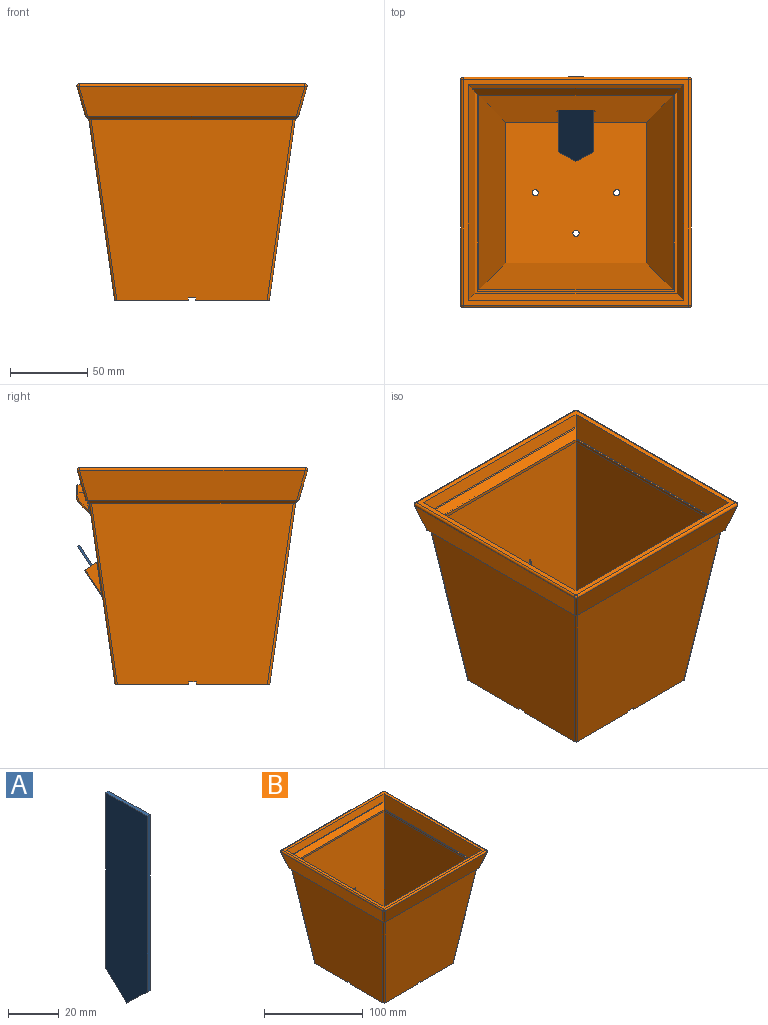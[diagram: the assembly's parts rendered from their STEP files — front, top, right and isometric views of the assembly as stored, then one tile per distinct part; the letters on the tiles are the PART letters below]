
ASSEMBLY  parts=2 mates=1
PART A: 7 faces, bbox 1.7x23x96 mm
  f0: plane 11.5x11mm, normal (0,-0.69,-0.72), area 26.3mm2, adj f1,f4,f5,f6
  f1: plane 11.5x11mm, normal (0,0.69,-0.72), area 26.3mm2, adj f0,f2,f5,f6
  f2: plane 85x1.65mm, normal (0,1,0), area 140.2mm2, adj f1,f3,f5,f6
  f3: plane 23x1.65mm, normal (0,0,1), area 37.9mm2, adj f2,f4,f5,f6
  f4: plane 85x1.65mm, normal (0,-1,0), area 140.2mm2, adj f0,f3,f5,f6
  f5: plane 96x23mm, normal (1,0,0), area 2081.5mm2, adj f0,f1,f2,f3,f4
  f6: plane 96x23mm, normal (-1,0,0), area 2081.5mm2, adj f0,f1,f2,f3,f4
PART B: 110 faces, bbox 149.1x150x140.2 mm
  f0: plane 11.53x6.95mm, normal (1,0,0), area 39.9mm2, adj f3,f19,f73,f95,f96,f97,f107
  f1: plane 11.53x6.95mm, normal (-1,0,0), area 39.9mm2, adj f19,f47,f73,f100,f102,f104,f109
  f2: plane 130.47x117.03mm, normal (0,0.99,-0.14), area 12611mm2, adj f3,f8,f16,f44,f47,f49,f53,f69
  f3: plane 62.79x2.2mm, normal (0,0.66,-0.76), area 170.1mm2, adj f0,f2,f19,f53,f56,f60,f96
  f4: plane 47.5x47.5mm, normal (0,0,-1), area 2255.8mm2, adj f5,f7,f11,f51,f72
  f5: plane 130.47x117.03mm, normal (0,-0.99,-0.14), area 13439.6mm2, adj f4,f10,f44,f46,f51,f66,f71,f72
  f6: plane 47.71x1.5mm, normal (0,1,0), area 71.4mm2, adj f10,f15,f44,f71
  f7: plane 47.71x1.5mm, normal (0,1,0), area 71.4mm2, adj f4,f11,f44,f72
  f8: plane 47.5x47.5mm, normal (0,0,-1), area 2255.8mm2, adj f2,f9,f15,f53,f69
  f9: plane 47.71x1.5mm, normal (0,-1,0), area 71.4mm2, adj f8,f15,f44,f69
  f10: plane 47.5x47.5mm, normal (0,0,-1), area 2255.8mm2, adj f5,f6,f15,f66,f71
  f11: plane 130.47x117.03mm, normal (-0.99,0,-0.14), area 13439.6mm2, adj f4,f7,f16,f43,f44,f48,f49,f51
  f12: plane 127.61x127.61mm, normal (0,0,1), area 379.8mm2, adj f27,f28,f30,f31,f32,f33,f39,f41
  f13: plane 139.58x7.5mm, normal (0,-0.96,0.28), area 1073.7mm2, adj f21,f24,f25,f42
  f14: plane 134.74x6.66mm, normal (0,-0.96,0.28), area 902.4mm2, adj f22,f24,f25,f40,f105
  f15: plane 130.47x117.03mm, normal (0.99,0,-0.14), area 13439.6mm2, adj f6,f8,f9,f10,f44,f45,f53,f66
  f16: plane 47.5x47.5mm, normal (0,0,-1), area 2255.8mm2, adj f2,f11,f43,f49,f70
  f17: plane 146x19.24mm, normal (0,-0.96,-0.28), area 2814.1mm2, adj f46,f57,f63,f67
  f18: plane 146x19.24mm, normal (0.96,0,-0.28), area 2814.1mm2, adj f45,f60,f64,f67
  f19: plane 146x19.24mm, normal (0,0.96,-0.28), area 2721.1mm2, adj f0,f1,f3,f47,f52,f59,f60,f73
  f20: plane 146x19.24mm, normal (-0.96,0,-0.28), area 2814.1mm2, adj f48,f52,f57,f58
  f21: plane 146x146mm, normal (0,0,1), area 1832.1mm2, adj f13,f23,f24,f25,f58,f59,f63,f64
  f22: plane 130.79x130.79mm, normal (0,0,1), area 819.2mm2, adj f14,f23,f24,f25,f29,f30,f31,f32
  f23: plane 139.58x15mm, normal (0,0.96,0.28), area 2113mm2, adj f21,f22,f24,f25
  f24: plane 139.58x15mm, normal (-0.96,0,0.28), area 2113mm2, adj f13,f14,f21,f22,f23,f41
  f25: plane 139.58x15mm, normal (0.96,0,0.28), area 2113mm2, adj f13,f14,f21,f22,f23,f39
  f26: plane 125.61x2mm, normal (0,-1,0), area 251.2mm2, adj f27,f33,f35,f42
  f27: plane 125.61x2mm, normal (-1,0,0), area 251.2mm2, adj f12,f26,f28,f38
  f28: plane 125.61x2mm, normal (0,1,0), area 251.2mm2, adj f12,f27,f33,f37
  f29: plane 127.61x2mm, normal (0,1,0), area 255.2mm2, adj f22,f30,f32,f40
  f30: plane 127.61x2mm, normal (-1,0,0), area 255.2mm2, adj f12,f22,f29,f31
  f31: plane 127.61x2mm, normal (0,-1,0), area 255.2mm2, adj f12,f22,f30,f32
  f32: plane 127.61x2mm, normal (1,0,0), area 255.2mm2, adj f12,f22,f29,f31
  f33: plane 125.61x2mm, normal (1,0,0), area 251.2mm2, adj f12,f26,f28,f36
  f34: plane 91.33x91.33mm, normal (0,0,1), area 8290.4mm2, adj f35,f36,f37,f38,f90,f91,f92,f93
  f35: plane 125.61x120mm, normal (0,-0.99,0.14), area 13000.7mm2, adj f26,f34,f36,f38,f79,f80,f81,f82
  f36: plane 125.61x120mm, normal (0.99,0,0.14), area 13148.5mm2, adj f33,f34,f35,f37
  f37: plane 125.61x120mm, normal (0,0.99,0.14), area 13148.5mm2, adj f28,f34,f36,f38
  f38: plane 125.61x120mm, normal (-0.99,0,0.14), area 13148.5mm2, adj f27,f34,f35,f37
  f39: plane 5.5x4.79mm, normal (-0.71,-0.71,0), area 5.4mm2, adj f12,f25,f40,f42
  f40: plane 134.63x4.54mm, normal (0,0.79,-0.61), area 752.2mm2, adj f14,f29,f39,f41
  f41: plane 5.5x4.79mm, normal (0.71,-0.71,0), area 5.4mm2, adj f12,f24,f40,f42
  f42: plane 135.19x5.5mm, normal (0,-0.75,0.66), area 950.8mm2, adj f13,f26,f39,f41
  f43: plane 47.71x1.5mm, normal (0,-1,0), area 71.4mm2, adj f11,f16,f44,f70
  f44: plane 100.43x100.43mm, normal (0,0,-1), area 929mm2, adj f2,f5,f6,f7,f9,f11,f15,f43
  f45: plane 135.54x2.2mm, normal (0.66,0,-0.76), area 368.4mm2, adj f15,f18,f53,f56,f60,f66,f67,f68
  f46: plane 135.54x2.2mm, normal (0,-0.66,-0.76), area 368.4mm2, adj f5,f17,f51,f54,f57,f66,f67,f68
  f47: plane 62.79x2.2mm, normal (0,0.66,-0.76), area 170.1mm2, adj f1,f2,f19,f49,f50,f52,f104
  f48: plane 135.54x2.2mm, normal (-0.66,0,-0.76), area 368.4mm2, adj f11,f20,f49,f50,f51,f52,f54,f57
  f49: cylinder r=1.5mm len=117.12mm, axis (0.14,-0.14,-0.98), area 277.5mm2, adj f2,f11,f16,f47,f48,f50
  f50: cylinder r=1.5mm len=3.07mm, axis (-0.6,0.6,0.52), area 4.9mm2, adj f47,f48,f49,f52
  f51: cylinder r=1.5mm len=117.12mm, axis (-0.14,-0.14,0.98), area 277.5mm2, adj f4,f5,f11,f46,f48,f54
  f52: cylinder r=1.5mm len=19.39mm, axis (-0.27,0.27,0.92), area 46.6mm2, adj f19,f20,f47,f48,f50,f55
  f53: cylinder r=1.5mm len=117.12mm, axis (0.14,0.14,0.98), area 277.5mm2, adj f2,f3,f8,f15,f45,f56
  f54: cylinder r=1.5mm len=3.07mm, axis (-0.6,-0.6,0.52), area 4.9mm2, adj f46,f48,f51,f57
  f55: sphere r=1.5mm, area 4.8mm2, adj f52,f58,f59
  f56: cylinder r=1.5mm len=3.07mm, axis (-0.6,-0.6,-0.52), area 4.9mm2, adj f3,f45,f53,f60
  f57: cylinder r=1.5mm len=19.39mm, axis (-0.27,-0.27,0.92), area 46.6mm2, adj f17,f20,f46,f48,f54,f61
  f58: cylinder r=1.5mm len=146mm, axis (0,-1,0), area 406.4mm2, adj f20,f21,f55,f61
  f59: cylinder r=1.5mm len=146mm, axis (-1,0,0), area 406.4mm2, adj f19,f21,f55,f62
  f60: cylinder r=1.5mm len=19.39mm, axis (0.27,0.27,0.92), area 46.6mm2, adj f3,f18,f19,f45,f56,f62
  f61: sphere r=1.5mm, area 4.8mm2, adj f57,f58,f63
  f62: sphere r=1.5mm, area 4.8mm2, adj f59,f60,f64
  f63: cylinder r=1.5mm len=146mm, axis (1,0,0), area 406.4mm2, adj f17,f21,f61,f65
  f64: cylinder r=1.5mm len=146mm, axis (0,1,0), area 406.4mm2, adj f18,f21,f62,f65
  f65: sphere r=1.5mm, area 4.8mm2, adj f63,f64,f67
  f66: cylinder r=1.5mm len=117.12mm, axis (-0.14,0.14,-0.98), area 277.5mm2, adj f5,f10,f15,f45,f46,f68
  f67: cylinder r=1.5mm len=19.39mm, axis (0.27,-0.27,0.92), area 46.6mm2, adj f17,f18,f45,f46,f65,f68
  f68: cylinder r=1.5mm len=3.07mm, axis (-0.6,0.6,-0.52), area 4.9mm2, adj f45,f46,f66,f67
  f69: plane 47.71x1.5mm, normal (-1,0,0), area 71.4mm2, adj f2,f8,f9,f44
  f70: plane 47.71x1.5mm, normal (1,0,0), area 71.4mm2, adj f2,f16,f43,f44
  f71: plane 47.71x1.5mm, normal (-1,0,0), area 71.4mm2, adj f5,f6,f10,f44
  f72: plane 47.71x1.5mm, normal (1,0,0), area 71.4mm2, adj f4,f5,f7,f44
  f73: cylinder r=5mm len=10mm, axis (0,1,0), area 44mm2, adj f0,f1,f19,f98
  f74: plane 8x6.93mm, normal (0,1,0), area 36mm2, adj f95,f98,f100,f105,f108
  f75: plane 20.96x10.49mm, normal (-1,0,0), area 85.9mm2, adj f78,f83,f84
  f76: plane 29x17.87mm, normal (0,0.84,-0.55), area 618.7mm2, adj f78,f83,f86,f89
  f77: plane 20.96x10.49mm, normal (1,0,0), area 85.9mm2, adj f78,f85,f86
  f78: plane 31.1x8.47mm, normal (0,0.55,0.84), area 237.5mm2, adj f2,f75,f76,f77,f79,f80,f81,f82
  f79: plane 25x21.13mm, normal (0,-0.84,0.55), area 630.9mm2, adj f35,f78,f80,f81
  f80: plane 22.5x13.79mm, normal (-1,0,0), area 56.4mm2, adj f35,f78,f79,f82
  f81: plane 22.5x13.79mm, normal (1,0,0), area 56.4mm2, adj f35,f78,f79,f82
  f82: plane 25x16.64mm, normal (0,0.84,-0.55), area 496.8mm2, adj f35,f78,f80,f81
  f83: cylinder r=0.5mm len=18.14mm, axis (0,-0.55,-0.84), area 16.1mm2, adj f75,f76,f78,f87
  f84: cylinder r=0.5mm len=21.26mm, axis (0,0.14,0.99), area 16.7mm2, adj f2,f75,f78,f87
  f85: cylinder r=0.5mm len=21.26mm, axis (0,-0.14,-0.99), area 16.7mm2, adj f2,f77,f78,f88
  f86: cylinder r=0.5mm len=18.14mm, axis (0,0.55,0.84), area 16.1mm2, adj f76,f77,f78,f88
  f87: bspline ~2.34x1mm, area 1.3mm2, adj f2,f83,f84,f89
  f88: bspline ~2.34x1mm, area 1.3mm2, adj f2,f85,f86,f89
  f89: cylinder r=0.5mm len=29mm, axis (-1,0,0), area 6.3mm2, adj f2,f76,f87,f88
  f90: cylinder r=2mm len=4mm, axis (0,0,-1), area 44mm2, adj f34,f44
  f91: cylinder r=2mm len=4mm, axis (0,0,-1), area 44mm2, adj f34,f44
  f92: cylinder r=2mm len=4mm, axis (0,0,-1), area 44mm2, adj f34,f44
  f93: cylinder r=2mm len=4mm, axis (0,0,-1), area 44mm2, adj f34,f44
  f94: plane 8x7.66mm, normal (0,0.71,-0.71), area 86.7mm2, adj f97,f101,f102,f108
  f95: cylinder r=1mm len=2.93mm, axis (0,0,1), area 4.6mm2, adj f0,f74,f98,f107
  f96: cylinder r=1mm len=5.87mm, axis (0,-0.14,-0.99), area 7.9mm2, adj f0,f2,f3,f99
  f97: cylinder r=1mm len=8.37mm, axis (0,0.71,0.71), area 15.5mm2, adj f0,f94,f99,f107
  f98: torus R=4mm, axis (0,-1,0), area 22.9mm2, adj f73,f74,f95,f100
  f99: bspline ~3.87x2.09mm, area 3.9mm2, adj f2,f96,f97,f101
  f100: cylinder r=1mm len=2.93mm, axis (0,0,-1), area 4.6mm2, adj f1,f74,f98,f109
  f101: cylinder r=1mm len=8mm, axis (-1,0,0), area 5.1mm2, adj f2,f94,f99,f103
  f102: cylinder r=1mm len=8.37mm, axis (0,-0.71,-0.71), area 15.5mm2, adj f1,f94,f103,f109
  f103: bspline ~3.87x2mm, area 3.9mm2, adj f2,f101,f102,f104
  f104: cylinder r=1mm len=5.87mm, axis (0,0.14,0.99), area 7.9mm2, adj f1,f2,f47,f103
  f105: cylinder r=2mm len=10.5mm, axis (0,1,0), area 128.1mm2, adj f14,f22,f74,f106
  f106: plane 4x3.16mm, normal (0,1,0), area 10.7mm2, adj f22,f105
  f107: torus R=4mm, axis (1,0,0), area 5.7mm2, adj f0,f95,f97,f108
  f108: cylinder r=5mm len=8mm, axis (1,0,0), area 31.4mm2, adj f74,f94,f107,f109
  f109: torus R=4mm, axis (-1,0,0), area 5.7mm2, adj f1,f100,f102,f108
PLACE A rot(axis=(-0.27,0.27,0.92),94.7deg) t=(-0.36,20.29,6.07)mm
PLACE B t=(-0.36,-0.06,-3.5)mm fixed
MATE fastened A.f6 <-> B.f82  axis (0,-0.84,0.55) through (-0.36,48,48.52)mm
